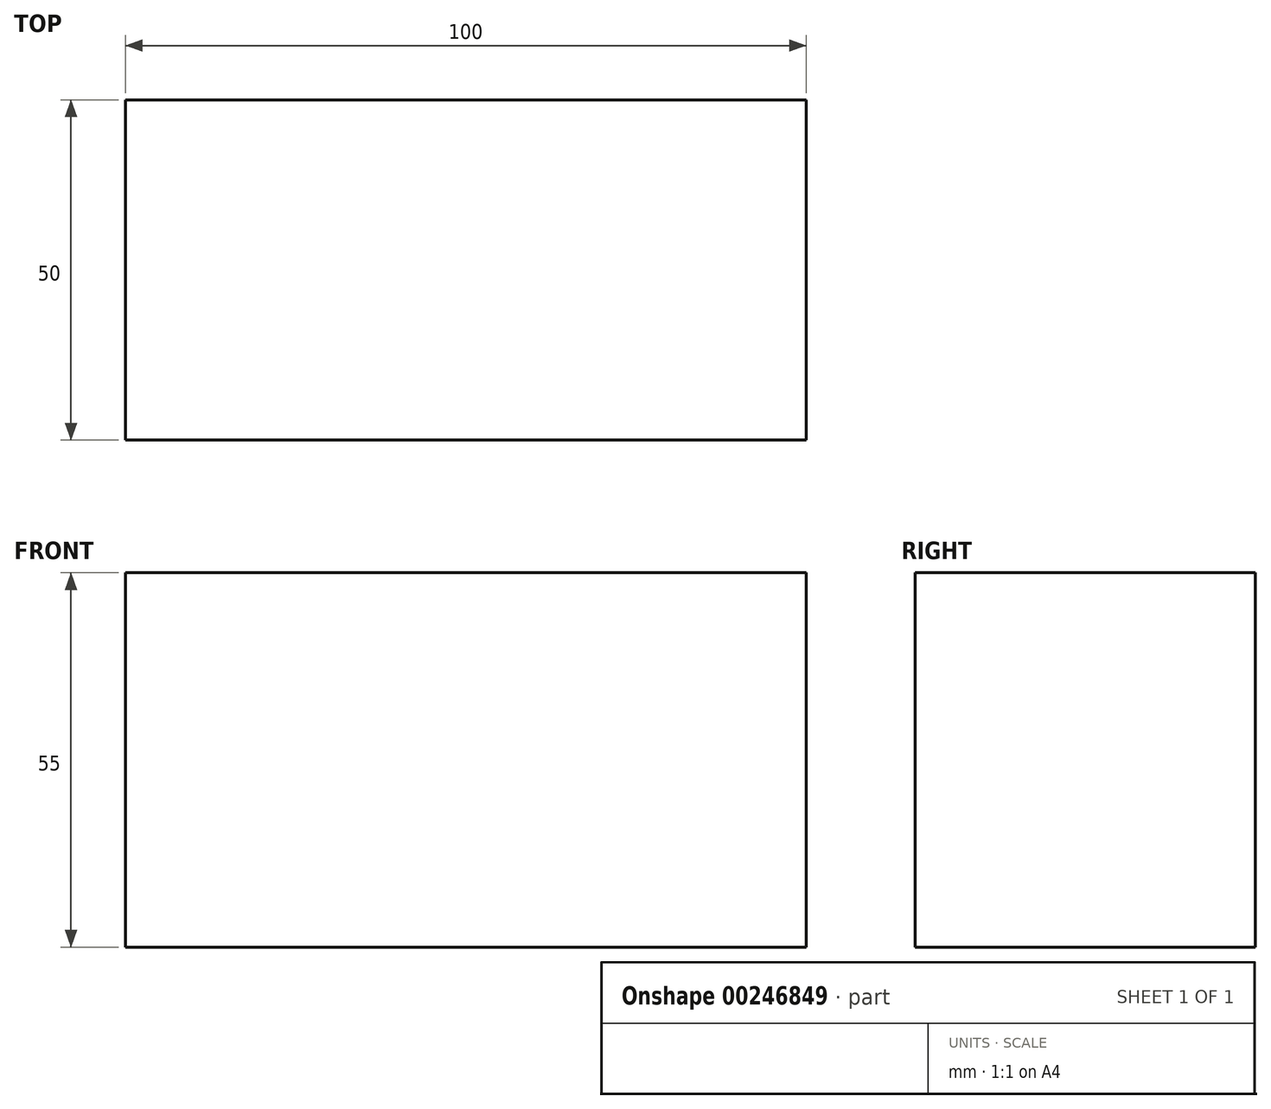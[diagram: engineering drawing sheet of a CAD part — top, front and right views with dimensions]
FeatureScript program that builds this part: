
annotation { "Feature Type Name" : "Feature", "Feature Type Description" : "" }
export const myFeature = defineFeature(function(context is Context, id is Id, definition is map)
    precondition{}
    {
        {
            var Q0;
            Q0=qCreatedBy(makeId("Front.planeOp"),FACE);
            var sketch = newSketch(context, id + "F0", { "sketchPlane" : qUnion([Q0])});
            skLineSegment(sketch, "E0.bottom", {"start": v(50, 27.5) * mm, "end": v(-50, 27.5) * mm});
            skLineSegment(sketch, "E0.top", {"start": v(50, -27.5) * mm, "end": v(-50, -27.5) * mm});
            skLineSegment(sketch, "E0.left", {"start": v(50, 27.5) * mm, "end": v(50, -27.5) * mm});
            skLineSegment(sketch, "E0.right", {"start": v(-50, 27.5) * mm, "end": v(-50, -27.5) * mm});
            skPoint(sketch, "E0.middle", {"position": v(0, 0) * mm});
            skSolve(sketch);
        }
        {
            var Q0;
            Q0=makeQuery(id+"F0.imprint","IMPRINT",FACE,{"disambiguationData":[TD([[makeQuery(id+"F0.imprint","IMPRINT",EDGE,{"derivedFrom":sQuery(id+"F0.wireOp",EDGE,"E0.bottom")}),1.0]])]});
            extrude(context, id + "F1", {"entities" : qUnion([Q0]), "depth" : 50 * mm});
        }
    });
